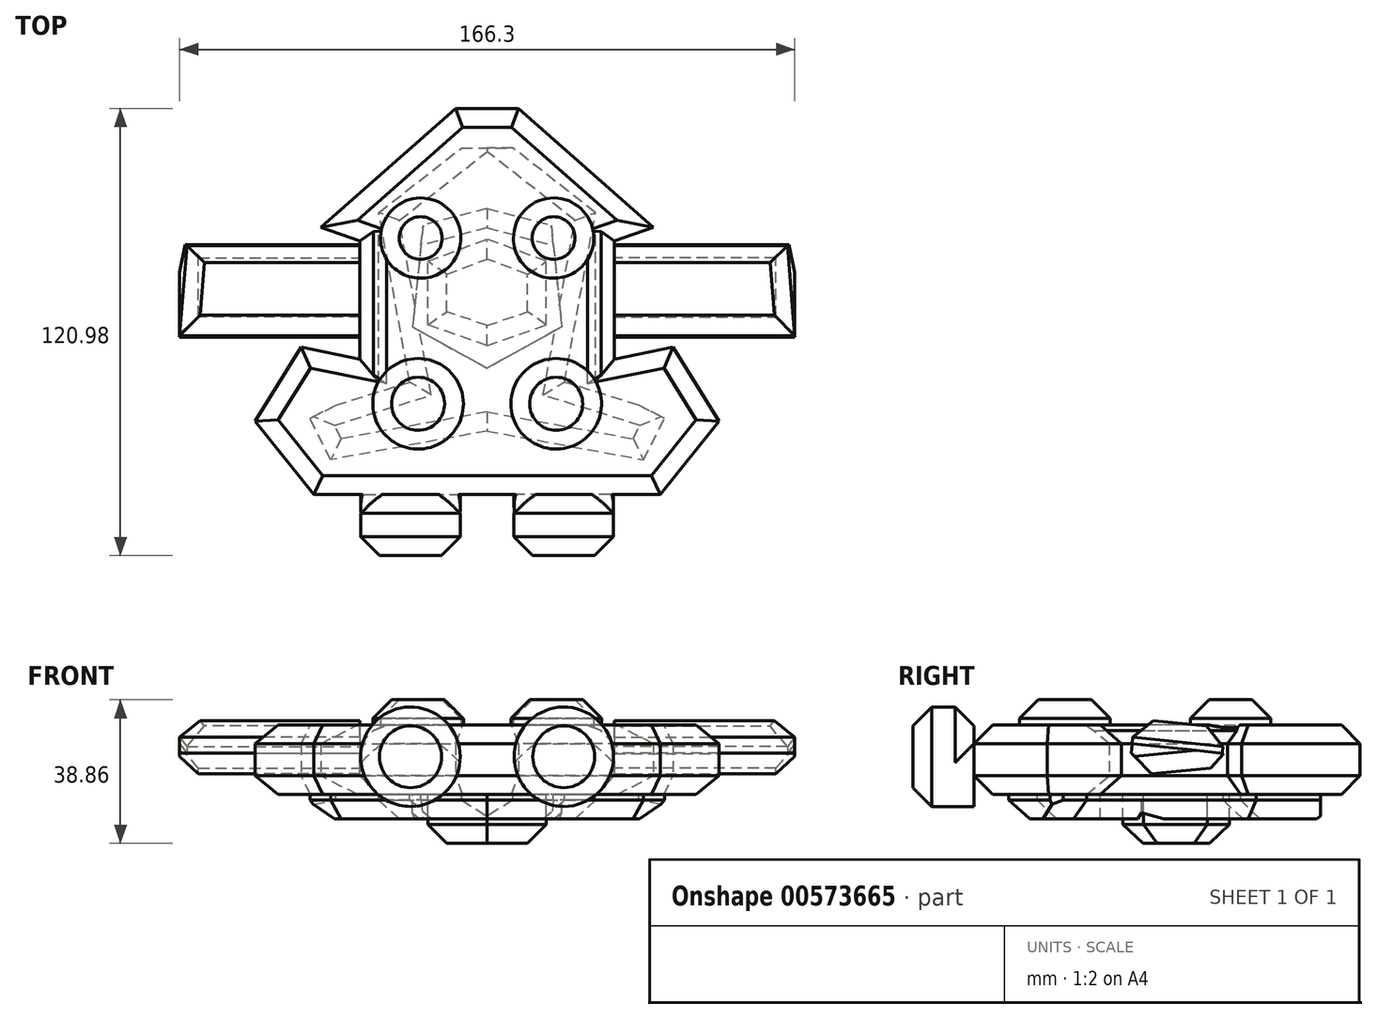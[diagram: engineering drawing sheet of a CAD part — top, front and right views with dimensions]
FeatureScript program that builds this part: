
annotation { "Feature Type Name" : "Feature", "Feature Type Description" : "" }
export const myFeature = defineFeature(function(context is Context, id is Id, definition is map)
    precondition{}
    {
        {
            var Q0;
            Q0=qCreatedBy(makeId("Top.planeOp"),FACE);
            var sketch = newSketch(context, id + "F0", { "sketchPlane" : qUnion([Q0])});
            skLineSegment(sketch, "E0", {"start": v(0, 48.08) * mm, "end": v(-8.5, 48.08) * mm});
            skLineSegment(sketch, "E1", {"start": v(-8.5, 48.08) * mm, "end": v(-44.96, 15.96) * mm});
            skLineSegment(sketch, "E2", {"start": v(-44.96, 15.96) * mm, "end": v(-34.38, 12.19) * mm});
            skLineSegment(sketch, "E3", {"start": v(-34.38, 12.19) * mm, "end": v(-34.38, -19.74) * mm});
            skLineSegment(sketch, "E4", {"start": v(-34.38, -19.74) * mm, "end": v(-50.25, -16.53) * mm});
            skLineSegment(sketch, "E5", {"start": v(-50.25, -16.53) * mm, "end": v(-62.72, -36.56) * mm});
            skLineSegment(sketch, "E6", {"start": v(-62.72, -36.56) * mm, "end": v(-46.85, -56.4) * mm});
            skLineSegment(sketch, "E7", {"start": v(-46.85, -56.4) * mm, "end": v(0, -56.4) * mm});
            skLineSegment(sketch, "E8", {"start": v(0, -56.4) * mm, "end": v(0, 48.08) * mm});
            skSolve(sketch);
        }
        {
            var Q0;
            Q0 = qSketchRegion(id + "F0", true);
            extrude(context, id + "F1", {"entities" : qUnion([Q0]), "depth" : 18.8 * mm, "offsetDistance" : 25.4 * mm});
        }
        {
            var Q0;
            Q0=makeQuery(id+"F1.opExtrude","CAP_EDGE",EDGE,{"disambiguationData":[OSD([sQuery(id+"F0.wireOp",EDGE,"E1")])],"isStart":false});
            var Q1;
            Q1=makeQuery(id+"F1.opExtrude","CAP_EDGE",EDGE,{"disambiguationData":[OSD([sQuery(id+"F0.wireOp",EDGE,"E0")])],"isStart":false});
            var Q2;
            Q2=makeQuery(id+"F1.opExtrude","CAP_EDGE",EDGE,{"disambiguationData":[OSD([sQuery(id+"F0.wireOp",EDGE,"E2")])],"isStart":false});
            var Q3;
            Q3=makeQuery(id+"F1.opExtrude","CAP_EDGE",EDGE,{"disambiguationData":[OSD([sQuery(id+"F0.wireOp",EDGE,"E3")])],"isStart":false});
            var Q4;
            Q4=makeQuery(id+"F1.opExtrude","CAP_EDGE",EDGE,{"disambiguationData":[OSD([sQuery(id+"F0.wireOp",EDGE,"E4")])],"isStart":false});
            var Q5;
            Q5=makeQuery(id+"F1.opExtrude","CAP_EDGE",EDGE,{"disambiguationData":[OSD([sQuery(id+"F0.wireOp",EDGE,"E5")])],"isStart":false});
            var Q6;
            Q6=makeQuery(id+"F1.opExtrude","CAP_EDGE",EDGE,{"disambiguationData":[OSD([sQuery(id+"F0.wireOp",EDGE,"E6")])],"isStart":false});
            var Q7;
            Q7=makeQuery(id+"F1.opExtrude","CAP_EDGE",EDGE,{"disambiguationData":[OSD([sQuery(id+"F0.wireOp",EDGE,"E7")])],"isStart":false});
            var Q8;
            Q8=makeQuery(id+"F1.opExtrude","CAP_EDGE",EDGE,{"disambiguationData":[OSD([sQuery(id+"F0.wireOp",EDGE,"E0")])],"isStart":true});
            var Q9;
            Q9=makeQuery(id+"F1.opExtrude","CAP_EDGE",EDGE,{"disambiguationData":[OSD([sQuery(id+"F0.wireOp",EDGE,"E1")])],"isStart":true});
            var Q10;
            Q10=makeQuery(id+"F1.opExtrude","CAP_EDGE",EDGE,{"disambiguationData":[OSD([sQuery(id+"F0.wireOp",EDGE,"E2")])],"isStart":true});
            var Q11;
            Q11=makeQuery(id+"F1.opExtrude","CAP_EDGE",EDGE,{"disambiguationData":[OSD([sQuery(id+"F0.wireOp",EDGE,"E3")])],"isStart":true});
            var Q12;
            Q12=makeQuery(id+"F1.opExtrude","CAP_EDGE",EDGE,{"disambiguationData":[OSD([sQuery(id+"F0.wireOp",EDGE,"E4")])],"isStart":true});
            var Q13;
            Q13=makeQuery(id+"F1.opExtrude","CAP_EDGE",EDGE,{"disambiguationData":[OSD([sQuery(id+"F0.wireOp",EDGE,"E5")])],"isStart":true});
            var Q14;
            Q14=makeQuery(id+"F1.opExtrude","CAP_EDGE",EDGE,{"disambiguationData":[OSD([sQuery(id+"F0.wireOp",EDGE,"E6")])],"isStart":true});
            var Q15;
            Q15=makeQuery(id+"F1.opExtrude","CAP_EDGE",EDGE,{"disambiguationData":[OSD([sQuery(id+"F0.wireOp",EDGE,"E7")])],"isStart":true});
            chamfer(context, id + "F2", {"entities" : qUnion([Q0, Q1, Q2, Q3, Q4, Q5, Q6, Q7, Q8, Q9, Q10, Q11, Q12, Q13, Q14, Q15]), "width" : 5.08 * mm, "tangentPropagation" : true});
        }
        {
            var Q0;
            Q0=makeQuery(id+"F1.opExtrude","CAP_FACE",FACE,{"disambiguationData":[OSD([sQuery(id+"F0.wireOp",EDGE,"E0"),sQuery(id+"F0.wireOp",EDGE,"E1"),sQuery(id+"F0.wireOp",EDGE,"E2"),sQuery(id+"F0.wireOp",EDGE,"E3"),sQuery(id+"F0.wireOp",EDGE,"E4"),sQuery(id+"F0.wireOp",EDGE,"E5"),sQuery(id+"F0.wireOp",EDGE,"E6"),sQuery(id+"F0.wireOp",EDGE,"E7"),sQuery(id+"F0.wireOp",EDGE,"E8")])],"isStart":false});
            var sketch = newSketch(context, id + "F3", { "sketchPlane" : qUnion([Q0])});
            skLineSegment(sketch, "E9", {"start": v(0, -39.19) * mm, "end": v(-42.3, -46.96) * mm});
            skLineSegment(sketch, "E10", {"start": v(-42.3, -46.96) * mm, "end": v(-47.96, -35.8) * mm});
            skLineSegment(sketch, "E11", {"start": v(-47.96, -35.8) * mm, "end": v(-40.94, -32.23) * mm});
            skLineSegment(sketch, "E12", {"start": v(-40.94, -32.23) * mm, "end": v(-20.93, -25.95) * mm});
            skLineSegment(sketch, "E13", {"start": v(-20.93, -25.95) * mm, "end": v(-29.3, 19.9) * mm});
            skLineSegment(sketch, "E14", {"start": v(-29.3, 19.9) * mm, "end": v(-6.94, 37.4) * mm});
            skLineSegment(sketch, "E15", {"start": v(-6.94, 37.4) * mm, "end": v(0, 37.4) * mm});
            skLineSegment(sketch, "E16", {"start": v(0, 37.4) * mm, "end": v(0, 15.77) * mm});
            skLineSegment(sketch, "E17", {"start": v(0, 15.77) * mm, "end": v(-17.9, 11.06) * mm});
            skLineSegment(sketch, "E18", {"start": v(-17.9, 11.06) * mm, "end": v(-20.18, -11.02) * mm});
            skLineSegment(sketch, "E19", {"start": v(-20.18, -11.02) * mm, "end": v(0, -22.2) * mm});
            skLineSegment(sketch, "E20", {"start": v(0, -22.2) * mm, "end": v(0, -39.19) * mm});
            skSolve(sketch);
        }
        {
            var Q0;
            Q0 = qSketchRegion(id + "F3", true);
            extrude(context, id + "F4", {"entities" : qUnion([Q0]), "operationType" : NewBodyOperationType.ADD, "oppositeDirection" : true, "depth" : 25.4 * mm, "offsetDistance" : 25.4 * mm});
        }
        {
            var Q0;
            Q0=makeQuery(id+"F4.opExtrude","CAP_EDGE",EDGE,{"disambiguationData":[OSD([sQuery(id+"F3.wireOp",EDGE,"E9")])],"isStart":false});
            var Q1;
            Q1=makeQuery(id+"F4.opExtrude","CAP_EDGE",EDGE,{"disambiguationData":[OSD([sQuery(id+"F3.wireOp",EDGE,"E10")])],"isStart":false});
            var Q2;
            Q2=makeQuery(id+"F4.opExtrude","CAP_EDGE",EDGE,{"disambiguationData":[OSD([sQuery(id+"F3.wireOp",EDGE,"E12")])],"isStart":false});
            var Q3;
            Q3=makeQuery(id+"F4.opExtrude","CAP_EDGE",EDGE,{"disambiguationData":[OSD([sQuery(id+"F3.wireOp",EDGE,"E14")])],"isStart":false});
            var Q4;
            Q4=makeQuery(id+"F4.opExtrude","CAP_EDGE",EDGE,{"disambiguationData":[OSD([sQuery(id+"F3.wireOp",EDGE,"E17")])],"isStart":false});
            var Q5;
            Q5=makeQuery(id+"F4.opExtrude","CAP_EDGE",EDGE,{"disambiguationData":[OSD([sQuery(id+"F3.wireOp",EDGE,"E13")])],"isStart":false});
            chamfer(context, id + "F5", {"entities" : qUnion([Q0, Q1, Q2, Q3, Q4, Q5]), "width" : 5.08 * mm, "tangentPropagation" : true});
        }
        {
            var Q0;
            {var subQ0=sQuery(id+"F0.wireOp",EDGE,"E8");Q0=makeQuery(id+"F4.boolean.opBoolean","SPLIT",FACE,{"disambiguationData":[TD([makeQuery(id+"F4.opExtrude","SWEPT_FACE",FACE,{"disambiguationData":[OSD([sQuery(id+"F3.wireOp",EDGE,"E17")])]})])],"derivedFrom":makeQuery(id+"F1.opExtrude","CAP_FACE",FACE,{"disambiguationData":[OSD([sQuery(id+"F0.wireOp",EDGE,"E0"),sQuery(id+"F0.wireOp",EDGE,"E1"),sQuery(id+"F0.wireOp",EDGE,"E2"),sQuery(id+"F0.wireOp",EDGE,"E3"),sQuery(id+"F0.wireOp",EDGE,"E4"),sQuery(id+"F0.wireOp",EDGE,"E5"),sQuery(id+"F0.wireOp",EDGE,"E6"),sQuery(id+"F0.wireOp",EDGE,"E7"),subQ0])],"isStart":true})});}
            var sketch = newSketch(context, id + "F6", { "sketchPlane" : qUnion([Q0])});
            skLineSegment(sketch, "E21", {"start": v(0, 16.06) * mm, "end": v(-16, 10.52) * mm});
            skLineSegment(sketch, "E22", {"start": v(-16, 10.52) * mm, "end": v(-16, -6.7) * mm});
            skLineSegment(sketch, "E23", {"start": v(-16, -6.7) * mm, "end": v(0, -12.75) * mm});
            skLineSegment(sketch, "E24", {"start": v(0, -12.75) * mm, "end": v(0, 16.06) * mm});
            skSolve(sketch);
        }
        {
            var Q0;
            Q0 = qSketchRegion(id + "F6", true);
            extrude(context, id + "F7", {"entities" : qUnion([Q0]), "operationType" : NewBodyOperationType.ADD, "depth" : 13.2 * mm, "offsetDistance" : 25.4 * mm});
        }
        {
            var Q0;
            Q0=makeQuery(id+"F7.opExtrude","CAP_EDGE",EDGE,{"disambiguationData":[OSD([sQuery(id+"F6.wireOp",EDGE,"E21")])],"isStart":false});
            var Q1;
            Q1=makeQuery(id+"F7.opExtrude","CAP_EDGE",EDGE,{"disambiguationData":[OSD([sQuery(id+"F6.wireOp",EDGE,"E22")])],"isStart":false});
            var Q2;
            Q2=makeQuery(id+"F7.opExtrude","CAP_EDGE",EDGE,{"disambiguationData":[OSD([sQuery(id+"F6.wireOp",EDGE,"E23")])],"isStart":false});
            var Q3;
            Q3=makeQuery(id+"F7.opExtrude","CAP_EDGE",EDGE,{"disambiguationData":[OSD([sQuery(id+"F6.wireOp",EDGE,"E22")])],"isStart":true});
            var Q4;
            Q4=makeQuery(id+"F7.opExtrude","CAP_EDGE",EDGE,{"disambiguationData":[OSD([sQuery(id+"F6.wireOp",EDGE,"E23")])],"isStart":true});
            var Q5;
            Q5=makeQuery(id+"F7.opExtrude","CAP_EDGE",EDGE,{"disambiguationData":[OSD([sQuery(id+"F6.wireOp",EDGE,"E21")])],"isStart":true});
            chamfer(context, id + "F8", {"entities" : qUnion([Q0, Q1, Q2, Q3, Q4, Q5]), "width" : 5.08 * mm, "tangentPropagation" : true});
        }
        {
            var Q0;
            Q0=makeQuery(id+"F1.opExtrude","SWEPT_FACE",FACE,{"disambiguationData":[OSD([sQuery(id+"F0.wireOp",EDGE,"E7")])]});
            var sketch = newSketch(context, id + "F9", { "sketchPlane" : qUnion([Q0])});
            skCircle(sketch, "E25", {"center": v(-20.74, 10.24) * mm, "radius": 13.46 * mm});
            skSolve(sketch);
        }
        {
            var Q0;
            Q0 = qSketchRegion(id + "F9", true);
            extrude(context, id + "F10", {"entities" : qUnion([Q0]), "operationType" : NewBodyOperationType.ADD, "depth" : 16.5 * mm, "offsetDistance" : 25.4 * mm});
        }
        {
            var Q0;
            Q0=makeQuery(id+"F10.opExtrude","CAP_EDGE",EDGE,{"disambiguationData":[OSD([sQuery(id+"F9.wireOp",EDGE,"E25")])],"isStart":false});
            var Q1;
            {var subQ0=sQuery(id+"F0.wireOp",EDGE,"E7");var subQ1=sQuery(id+"F9.wireOp",EDGE,"E25");var subQ2=makeQuery(id+"F10.opExtrude","SWEPT_FACE",FACE,{"disambiguationData":[OSD([subQ1])]});var subQ3=makeQuery(id+"F10.opExtrude","CAP_FACE",FACE,{"disambiguationData":[OSD([subQ1])],"isStart":true});Q1=makeQuery(id+"F10.boolean.opBoolean","SPLIT",EDGE,{"disambiguationData":[topologyDisambiguationEdgeConnected([subQ2,subQ3]),TD([makeQuery(id+"F2.opChamfer","BLEND_FACE",FACE,{"disambiguationData":[OSD([subQ0]),TDD([makeQuery(id+"F1.opExtrude","CAP_EDGE",EDGE,{"disambiguationData":[OSD([subQ0])],"isStart":false})])]})])],"derivedFrom":makeQuery(id+"F10.opExtrude","CAP_EDGE",EDGE,{"disambiguationData":[OSD([subQ1])],"isStart":true})});}
            chamfer(context, id + "F11", {"entities" : qUnion([Q0, Q1]), "width" : 5.08 * mm, "tangentPropagation" : true});
        }
        {
            var Q0;
            Q0=makeQuery(id+"F1.opExtrude","CAP_FACE",FACE,{"disambiguationData":[OSD([sQuery(id+"F0.wireOp",EDGE,"E0"),sQuery(id+"F0.wireOp",EDGE,"E1"),sQuery(id+"F0.wireOp",EDGE,"E2"),sQuery(id+"F0.wireOp",EDGE,"E3"),sQuery(id+"F0.wireOp",EDGE,"E4"),sQuery(id+"F0.wireOp",EDGE,"E5"),sQuery(id+"F0.wireOp",EDGE,"E6"),sQuery(id+"F0.wireOp",EDGE,"E7"),sQuery(id+"F0.wireOp",EDGE,"E8")])],"isStart":false});
            var sketch = newSketch(context, id + "F12", { "sketchPlane" : qUnion([Q0])});
            skCircle(sketch, "E26", {"center": v(-18.68, -31.83) * mm, "radius": 12.26 * mm});
            skCircle(sketch, "E27", {"center": v(-17.97, 13) * mm, "radius": 10.86 * mm});
            skSolve(sketch);
        }
        {
            var Q0;
            Q0 = qSketchRegion(id + "F12", true);
            extrude(context, id + "F13", {"entities" : qUnion([Q0]), "operationType" : NewBodyOperationType.ADD, "depth" : 6.86 * mm, "offsetDistance" : 25.4 * mm});
        }
        {
            var Q0;
            Q0=makeQuery(id+"F13.opExtrude","CAP_EDGE",EDGE,{"disambiguationData":[OSD([sQuery(id+"F12.wireOp",EDGE,"E27")])],"isStart":false});
            var Q1;
            Q1=makeQuery(id+"F13.opExtrude","CAP_FACE",FACE,{"disambiguationData":[OSD([sQuery(id+"F12.wireOp",EDGE,"E26")])],"isStart":false});
            var Q2;
            {var subQ0=sQuery(id+"F0.wireOp",EDGE,"E3");var subQ1=makeQuery(id+"F1.opExtrude","CAP_FACE",FACE,{"disambiguationData":[OSD([sQuery(id+"F0.wireOp",EDGE,"E0"),sQuery(id+"F0.wireOp",EDGE,"E1"),sQuery(id+"F0.wireOp",EDGE,"E2"),subQ0,sQuery(id+"F0.wireOp",EDGE,"E4"),sQuery(id+"F0.wireOp",EDGE,"E5"),sQuery(id+"F0.wireOp",EDGE,"E6"),sQuery(id+"F0.wireOp",EDGE,"E7"),sQuery(id+"F0.wireOp",EDGE,"E8")])],"isStart":false});var subQ2=makeQuery(id+"F1.opExtrude","CAP_EDGE",EDGE,{"disambiguationData":[OSD([subQ0])],"isStart":false});Q2=makeQuery(id+"F13.boolean.opBoolean","SPLIT",EDGE,{"disambiguationData":[topologyDisambiguationEdgeConnected([subQ1])],"derivedFrom":makeQuery(id+"F2.opChamfer","BLEND_EDGE",EDGE,{"blendedFrom":[subQ2,subQ1],"blendedInto":[subQ1]})});}
            chamfer(context, id + "F14", {"entities" : qUnion([Q0, Q1, Q2]), "width" : 5.08 * mm, "tangentPropagation" : true});
        }
        {
            var Q0;
            Q0=makeQuery(id+"F1.opExtrude","SWEPT_FACE",FACE,{"disambiguationData":[OSD([sQuery(id+"F0.wireOp",EDGE,"E3")])]});
            var sketch = newSketch(context, id + "F15", { "sketchPlane" : qUnion([Q0])});
            skLineSegment(sketch, "E28", {"start": v(-12.19, 11.05) * mm, "end": v(13.6, 13.72) * mm});
            skLineSegment(sketch, "E29", {"start": v(13.6, 13.72) * mm, "end": v(14.5, 5.08) * mm});
            skLineSegment(sketch, "E30", {"start": v(14.5, 5.08) * mm, "end": v(-12.19, 7.65) * mm});
            skLineSegment(sketch, "E31", {"start": v(-12.19, 7.65) * mm, "end": v(-12.19, 11.05) * mm});
            skSolve(sketch);
        }
        {
            var Q0;
            Q0 = qSketchRegion(id + "F15", true);
            extrude(context, id + "F16", {"entities" : qUnion([Q0]), "operationType" : NewBodyOperationType.ADD, "depth" : 48.77 * mm, "offsetDistance" : 25.4 * mm});
        }
        {
            var Q0;
            Q0=makeQuery(id+"F16.opExtrude","SWEPT_EDGE",EDGE,{"disambiguationData":[OSD([sQuery(id+"F0.wireOp",EDGE,"E2"),sQuery(id+"F0.wireOp",EDGE,"E3"),sQuery(id+"F15.wireOp",EDGE,"E30"),sQuery(id+"F15.wireOp",EDGE,"E31")])]});
            var Q1;
            Q1=makeQuery(id+"F16.opExtrude","SWEPT_EDGE",EDGE,{"disambiguationData":[OSD([sQuery(id+"F0.wireOp",EDGE,"E3"),sQuery(id+"F15.wireOp",EDGE,"E29"),sQuery(id+"F15.wireOp",EDGE,"E30")])]});
            var Q2;
            Q2=makeQuery(id+"F16.opExtrude","CAP_EDGE",EDGE,{"disambiguationData":[OSD([sQuery(id+"F15.wireOp",EDGE,"E30")])],"isStart":false});
            chamfer(context, id + "F17", {"entities" : qUnion([Q0, Q1, Q2]), "width" : 5.08 * mm, "tangentPropagation" : true});
        }
        {
            var Q0;
            Q0=makeQuery(id+"F16.opExtrude","SWEPT_FACE",FACE,{"disambiguationData":[OSD([sQuery(id+"F15.wireOp",EDGE,"E28")])]});
            var sketch = newSketch(context, id + "F18", { "sketchPlane" : qUnion([Q0])});
            skLineSegment(sketch, "E32", {"start": v(-34.38, 9.58) * mm, "end": v(-34.38, -14.94) * mm});
            skLineSegment(sketch, "E33", {"start": v(-34.38, -14.94) * mm, "end": v(-83.15, -14.94) * mm});
            skLineSegment(sketch, "E34", {"start": v(-83.15, -14.94) * mm, "end": v(-81.22, 9.58) * mm});
            skLineSegment(sketch, "E35", {"start": v(-81.22, 9.58) * mm, "end": v(-34.38, 9.58) * mm});
            skSolve(sketch);
        }
        {
            var Q0;
            Q0 = qSketchRegion(id + "F18", true);
            extrude(context, id + "F19", {"entities" : qUnion([Q0]), "operationType" : NewBodyOperationType.ADD, "depth" : 6.86 * mm, "offsetDistance" : 25.4 * mm});
        }
        {
            var Q0;
            Q0=makeQuery(id+"F19.opExtrude","CAP_EDGE",EDGE,{"disambiguationData":[OSD([sQuery(id+"F18.wireOp",EDGE,"E34")])],"isStart":false});
            var Q1;
            Q1=makeQuery(id+"F19.opExtrude","CAP_EDGE",EDGE,{"disambiguationData":[OSD([sQuery(id+"F18.wireOp",EDGE,"E33")])],"isStart":false});
            var Q2;
            Q2=makeQuery(id+"F19.opExtrude","CAP_EDGE",EDGE,{"disambiguationData":[OSD([sQuery(id+"F18.wireOp",EDGE,"E35")])],"isStart":false});
            chamfer(context, id + "F20", {"entities" : qUnion([Q0, Q1, Q2]), "width" : 5.08 * mm, "tangentPropagation" : true});
        }
        {
            var Q0;
            Q0=makeQuery(id+"F1.opExtrude","SWEPT_BODY",BODY,{"disambiguationData":[OSD([sQuery(id+"F0.wireOp",EDGE,"E0"),sQuery(id+"F0.wireOp",EDGE,"E1"),sQuery(id+"F0.wireOp",EDGE,"E2"),sQuery(id+"F0.wireOp",EDGE,"E3"),sQuery(id+"F0.wireOp",EDGE,"E4"),sQuery(id+"F0.wireOp",EDGE,"E5"),sQuery(id+"F0.wireOp",EDGE,"E6"),sQuery(id+"F0.wireOp",EDGE,"E7"),sQuery(id+"F0.wireOp",EDGE,"E8")])]});
            var Q1;
            Q1=qCreatedBy(makeId("Right.planeOp"),FACE);
            mirror(context, id + "F21", {"operationType" : NewBodyOperationType.ADD, "entities" : qUnion([Q0]), "mirrorPlane" : qUnion([Q1])});
        }
    });
